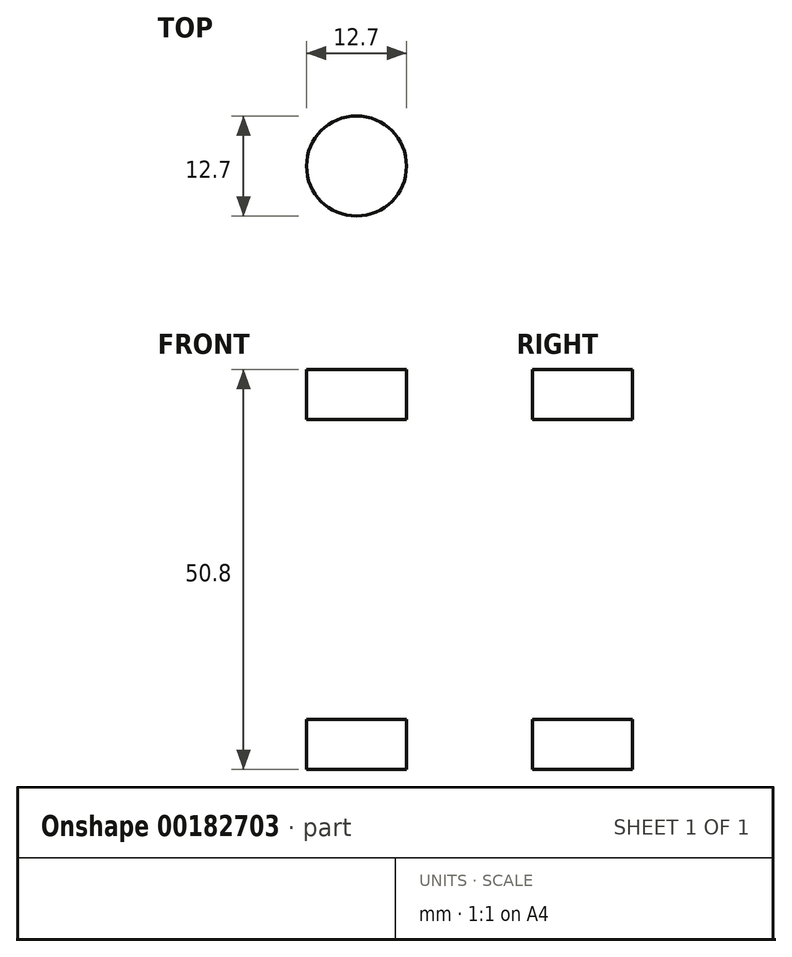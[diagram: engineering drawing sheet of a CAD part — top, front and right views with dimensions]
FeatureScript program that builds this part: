
annotation { "Feature Type Name" : "Feature", "Feature Type Description" : "" }
export const myFeature = defineFeature(function(context is Context, id is Id, definition is map)
    precondition{}
    {
        {
            var Q0;
            Q0=qCreatedBy(makeId("Front.planeOp"),FACE);
            var sketch = newSketch(context, id + "F0", { "sketchPlane" : qUnion([Q0])});
            skLineSegment(sketch, "E0.bottom", {"start": v(-50.8, 0) * mm, "end": v(50.8, 0) * mm});
            skLineSegment(sketch, "E0.top", {"start": v(-50.8, 50.8) * mm, "end": v(50.8, 50.8) * mm});
            skLineSegment(sketch, "E0.left", {"start": v(-50.8, 0) * mm, "end": v(-50.8, 50.8) * mm});
            skLineSegment(sketch, "E0.right", {"start": v(50.8, 0) * mm, "end": v(50.8, 50.8) * mm});
            skLineSegment(sketch, "E1.0", {"start": v(-44.45, 44.45) * mm, "end": v(44.45, 44.45) * mm});
            skLineSegment(sketch, "E1.1", {"start": v(-44.45, 6.35) * mm, "end": v(-44.45, 44.45) * mm});
            skLineSegment(sketch, "E1.2", {"start": v(-44.45, 6.35) * mm, "end": v(44.45, 6.35) * mm});
            skLineSegment(sketch, "E1.3", {"start": v(44.45, 6.35) * mm, "end": v(44.45, 44.45) * mm});
            skSolve(sketch);
        }
        {
            var Q0;
            Q0=makeQuery(id+"F0.imprint","IMPRINT",FACE,{"disambiguationData":[TD([[makeQuery(id+"F0.imprint","IMPRINT",EDGE,{"derivedFrom":sQuery(id+"F0.wireOp",EDGE,"E0.bottom")}),1.0]])]});
            extrude(context, id + "F1", {"entities" : qUnion([Q0]), "depth" : 101.6 * mm});
        }
        {
            var Q0;
            Q0=makeQuery(id+"F1.opExtrude","SWEPT_FACE",FACE,{"disambiguationData":[OSD([sQuery(id+"F0.wireOp",EDGE,"E0.top")])]});
            var sketch = newSketch(context, id + "F2", { "sketchPlane" : qUnion([Q0])});
            skCircle(sketch, "E2", {"center": v(25.4, -76.2) * mm, "radius": 6.35 * mm});
            skCircle(sketch, "E3.MirrorC", {"center": v(-25.4, -76.2) * mm, "radius": 6.35 * mm});
            skSolve(sketch);
        }
        {
            var Q0;
            Q0=makeQuery(id+"F2.imprint","IMPRINT",FACE,{"disambiguationData":[TD([[makeQuery(id+"F2.imprint","IMPRINT",EDGE,{"derivedFrom":sQuery(id+"F2.wireOp",EDGE,"E2")}),1.0]])]});
            var Q1;
            Q1=makeQuery(id+"F2.imprint","IMPRINT",FACE,{"disambiguationData":[TD([[makeQuery(id+"F2.imprint","IMPRINT",EDGE,{"derivedFrom":sQuery(id+"F2.wireOp",EDGE,"E3.MirrorC")}),-1.0]])]});
            extrude(context, id + "F3", {"entities" : qUnion([Q0, Q1]), "operationType" : NewBodyOperationType.REMOVE, "endBound" : BoundingType.THROUGH_ALL, "oppositeDirection" : true, "depth" : 25.4 * mm});
        }
    });
